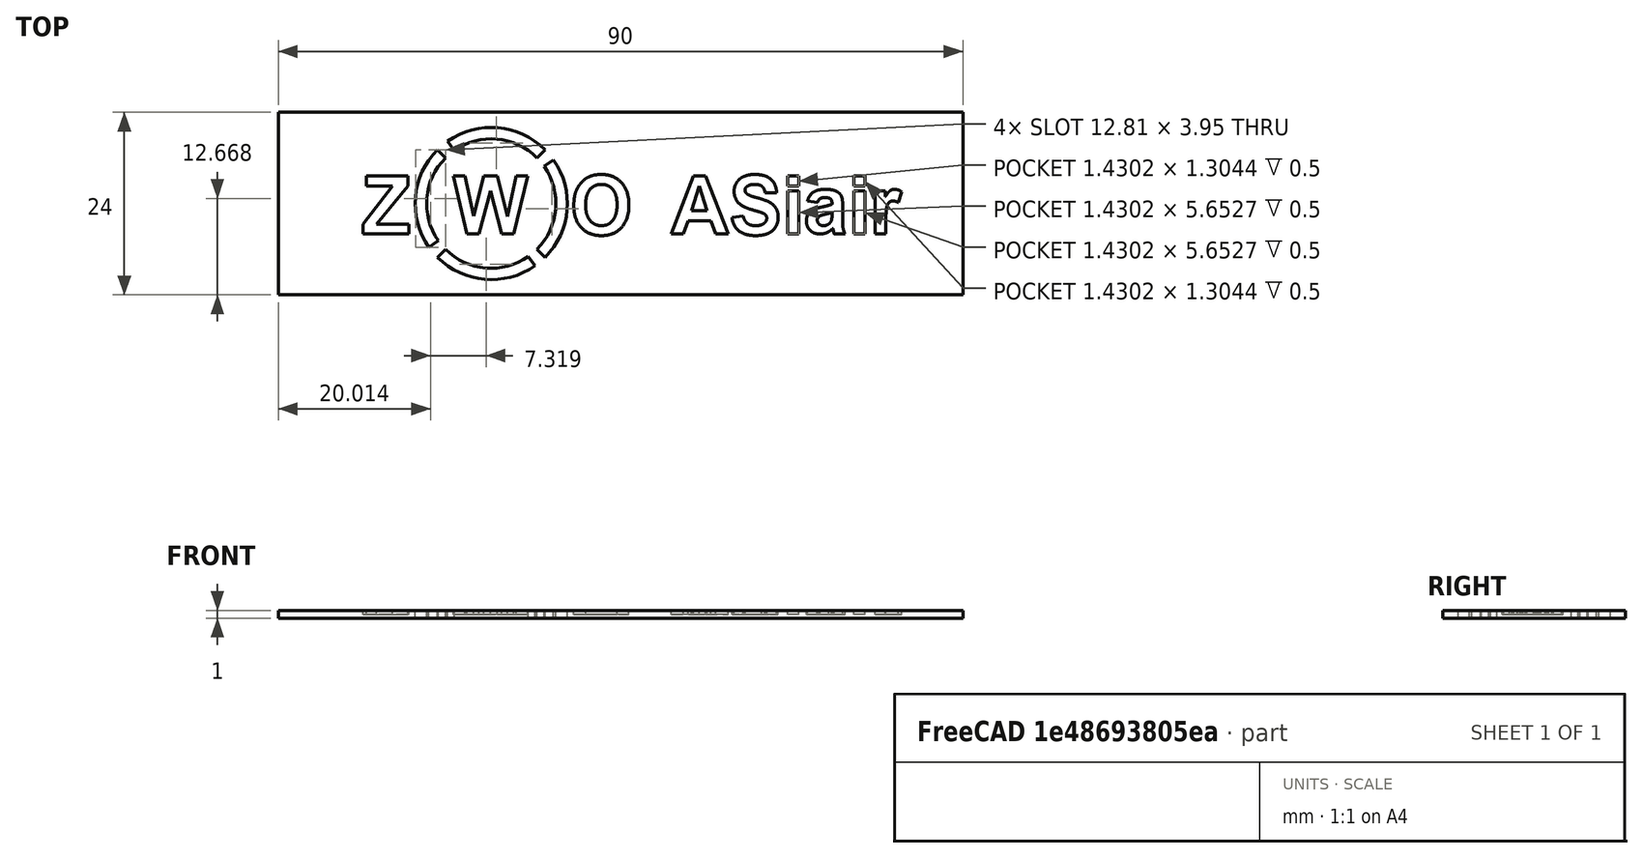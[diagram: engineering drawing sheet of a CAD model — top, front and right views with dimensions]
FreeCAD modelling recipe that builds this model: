
FCSTD DOCUMENT  (FreeCAD 0.18R4 (GitTag))
Label: ZWOASIAIR
License: All rights reserved
LicenseURL: http://en.wikipedia.org/wiki/All_rights_reserved
objects: Part::Cylinder×8, Part::Cut×5, Part::MultiFuse×2, Part::Box×1, Part::Part2DObjectPython×1, Part::Extrusion×1
note: 18 computed .brp shape members not serialized (recipe doc carries the construction recipe); baked Part::Feature solids carry a one-line shape summary decoded from their .brp

FEATURE [Part::Box] Box  label="Krychle"
  AttacherType = Attacher::AttachEngine3D
  Height = 1
  Length = 90
  Placement = pos=(0,-12,0) rot=(0,0,1;0rad)
  Width = 24
FEATURE [Part::Cylinder] Cylinder  label="Válec"
  Angle = 80
  AttacherType = Attacher::AttachEngine3D
  Height = 1
  Radius = 10
FEATURE [Part::Cylinder] Cylinder001  label="Válec001"
  Angle = 80
  AttacherType = Attacher::AttachEngine3D
  Height = 1
  Radius = 8.5
FEATURE [Part::Cut] Cut
  Base = -> Cylinder
  Tool = -> Cylinder001
FEATURE [Part::Cylinder] Cylinder002  label="Válec002"
  Angle = 80
  AttacherType = Attacher::AttachEngine3D
  Height = 1
  Radius = 10
FEATURE [Part::Cylinder] Cylinder003  label="Válec003"
  Angle = 80
  AttacherType = Attacher::AttachEngine3D
  Height = 1
  Radius = 8.5
FEATURE [Part::Cut] Cut001
  Base = -> Cylinder002
  Placement = pos=(0,0,0) rot=(0,0,1;1.5708rad)
  Tool = -> Cylinder003
FEATURE [Part::Cylinder] Cylinder004  label="Válec004"
  Angle = 80
  AttacherType = Attacher::AttachEngine3D
  Height = 1
  Radius = 8.5
FEATURE [Part::Cylinder] Cylinder005  label="Válec005"
  Angle = 80
  AttacherType = Attacher::AttachEngine3D
  Height = 1
  Radius = 10
FEATURE [Part::Cut] Cut002
  Base = -> Cylinder005
  Placement = pos=(0,0,0) rot=(0,0,1;3.14159rad)
  Tool = -> Cylinder004
FEATURE [Part::Cylinder] Cylinder006  label="Válec006"
  Angle = 80
  AttacherType = Attacher::AttachEngine3D
  Height = 1
  Radius = 8.5
FEATURE [Part::Cylinder] Cylinder007  label="Válec007"
  Angle = 80
  AttacherType = Attacher::AttachEngine3D
  Height = 1
  Radius = 10
FEATURE [Part::Cut] Cut003
  Base = -> Cylinder007
  Placement = pos=(0,0,0) rot=(0,0,1;-1.5708rad)
  Tool = -> Cylinder006
FEATURE [Part::MultiFuse] Fusion
  Placement = pos=(28,0,0) rot=(0,0,1;0.785398rad)
  Shapes = -> [Cut,Cut003,Cut002,Cut001]
FEATURE [Part::Part2DObjectPython] ShapeString  # Draft 2D object (typed FeaturePython)
  FontFile = <path>
  Placement = pos=(11,-4,1) rot=(0,0,1;0rad)
  Size = 8
  String = Z  W  O  ASiair
  Tracking = 0
FEATURE [Part::Extrusion] Extrude
  Base = -> ShapeString
  Dir = (0,0,1)
  DirMode = 2
  FaceMakerClass = Part::FaceMakerBullseye
  LengthFwd = 1
  LengthRev = 0
  Placement = pos=(0,0,-0.5) rot=(0,0,1;0rad)
  Solid = true
  Symmetric = false
FEATURE [Part::MultiFuse] Fusion001
  Shapes = -> [Fusion,Extrude]
FEATURE [Part::Cut] Cut004
  Base = -> Box
  Tool = -> Fusion001
note: 1 file-system path scrubbed to <path> (originals preserved in the JSON sidecar)
